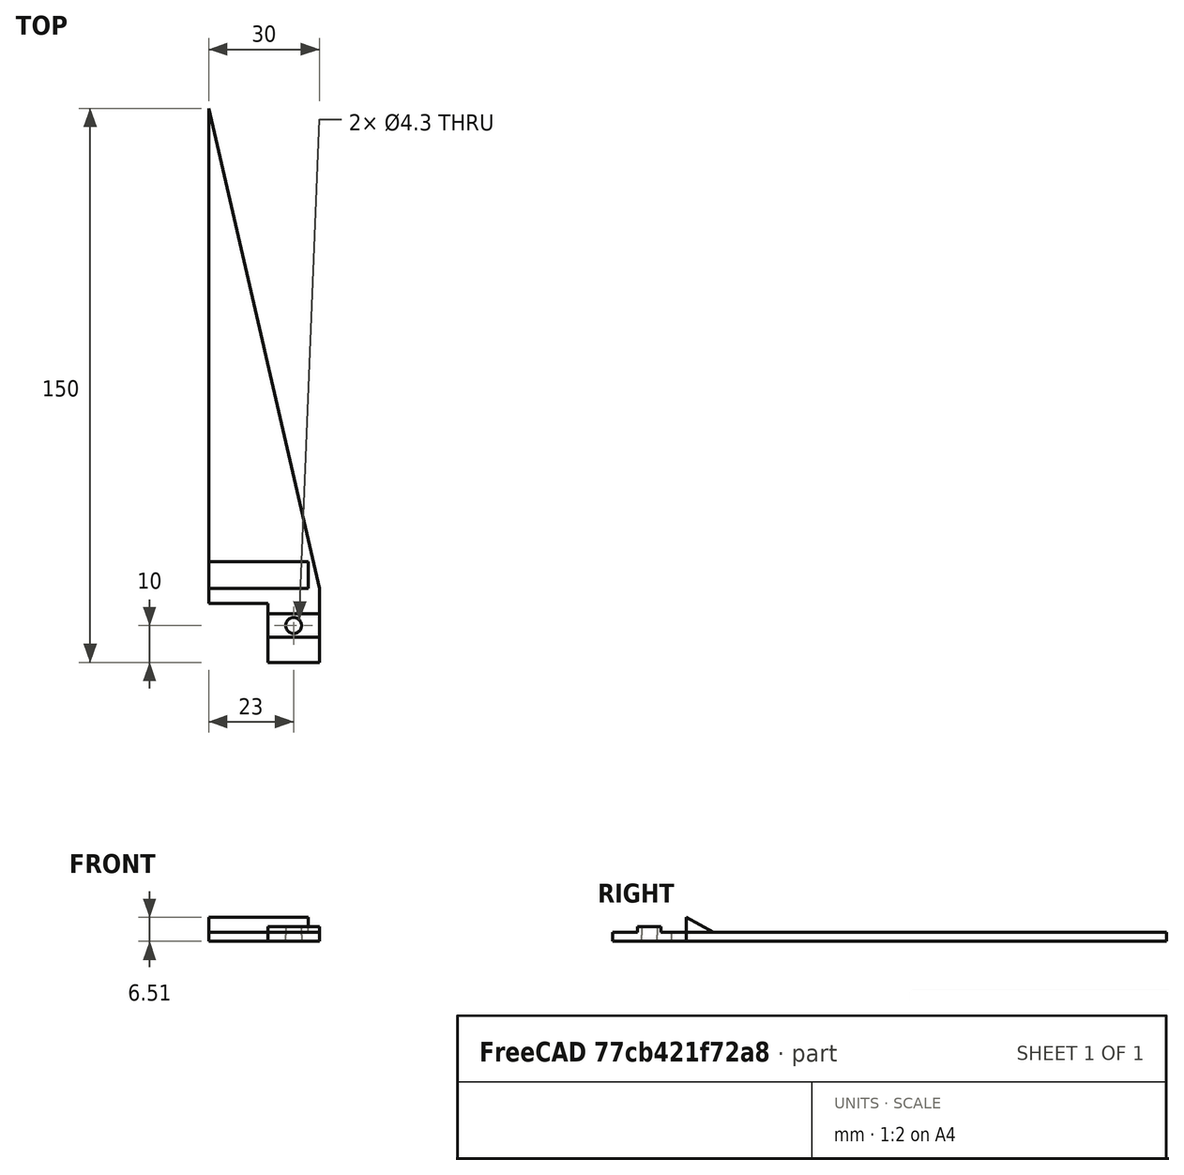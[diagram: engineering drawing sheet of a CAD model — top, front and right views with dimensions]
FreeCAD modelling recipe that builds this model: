
FCSTD DOCUMENT  (FreeCAD 0.19R)
Label: SimplePointe.r
License: All rights reserved
LicenseURL: http://en.wikipedia.org/wiki/All_rights_reserved
objects: Sketcher::SketchObject×6, PartDesign::Pad×3, PartDesign::Pocket×3, Mesh::Feature×2, PartDesign::Body×1
note: 19 computed .brp shape members not serialized (recipe doc carries the construction recipe); baked Part::Feature solids carry a one-line shape summary decoded from their .brp

FEATURE [Sketcher::SketchObject] Sketch
  FullyConstrained = true
  MapMode = 5
  Support = -> [XY_Plane]
  sketch-geometry (4):
    g0: LineSegment StartX=0 StartY=-20 StartZ=0 EndX=0 EndY=130 EndZ=0
    g1: LineSegment StartX=0 StartY=130 StartZ=0 EndX=30 EndY=0 EndZ=0
    g2: LineSegment StartX=30 StartY=0 StartZ=0 EndX=30 EndY=-20 EndZ=0
    g3: LineSegment StartX=30 StartY=-20 StartZ=0 EndX=0 EndY=-20 EndZ=0
  constraints (12):
    c: Vertical(g0)
    c: Coincident(g0,g1)
    c: PointOnObject(g1,g-1)
    c: Coincident(g1,g2)
    c: Coincident(g2,g3)
    c: Coincident(g3,g0)
    c: Horizontal(g3)
    c: Vertical(g2)
    c: Distance(g2) = 20
    c: PointOnObject(g0,g-2)
    c: Distance(g3) = 30
    c: Distance(g0) = 150
FEATURE [PartDesign::Pad] Pad
  Direction = (1,1,1)
  Length = 2.5
  Length2 = 100
  Profile = -> Sketch
  Type = 0
FEATURE [Sketcher::SketchObject] Sketch001
  FullyConstrained = false
  MapMode = 5
  Placement = pos=(0,0,2.5) rot=(0,0,1;0rad)
  Support = -> [Pad]
  sketch-geometry (4):
    g0: LineSegment StartX=-3.88556 StartY=-4 StartZ=0 EndX=16 EndY=-4 EndZ=0
    g1: LineSegment StartX=16 StartY=-4 StartZ=0 EndX=16 EndY=-24.7897 EndZ=0
    g2: LineSegment StartX=16 StartY=-24.7897 StartZ=0 EndX=-5.29231 EndY=-24.7897 EndZ=0
    g3: LineSegment StartX=-5.29231 StartY=-24.7897 StartZ=0 EndX=-3.88556 EndY=-4 EndZ=0
  constraints (9):
    c: Horizontal(g0)
    c: Coincident(g0,g1)
    c: Coincident(g1,g2)
    c: Horizontal(g2)
    c: Coincident(g2,g3)
    c: Coincident(g3,g0)
    c: DistanceX(g0) = 16
    c: DistanceY(g0) = -4
    c: Vertical(g1)
FEATURE [PartDesign::Pocket] Pocket
  BaseFeature = -> Pad
  Length = 5
  Length2 = 100
  Profile = -> Sketch001
  Type = 1
FEATURE [Sketcher::SketchObject] Sketch002
  FullyConstrained = true
  MapMode = 5
  Placement = pos=(0,0,2.5) rot=(0,0,1;0rad)
  Support = -> [Pocket]
  sketch-geometry (1):
    g0: Circle CenterX=23 CenterY=-10 CenterZ=0 NormalX=0 NormalY=0 NormalZ=1 AngleXU=0 Radius=2.15
  constraints (3):
    c: DistanceY(g0) = -10
    c: Diameter(g0) = 4.3
    c: DistanceX(g0) = 23
FEATURE [PartDesign::Pocket] Pocket001
  BaseFeature = -> Pocket
  Length = 5
  Length2 = 100
  Profile = -> Sketch002
  Type = 1
FEATURE [Sketcher::SketchObject] Sketch003
  FullyConstrained = false
  MapMode = 5
  Placement = pos=(0,0,0) rot=(0.57735,-0.57735,-0.57735;2.0944rad)
  Support = -> [Pocket001]
  sketch-geometry (3):
    g0: LineSegment StartX=0 StartY=6.51026 StartZ=0 EndX=-7.95 EndY=2.16643 EndZ=0
    g1: LineSegment StartX=-7.95 StartY=2.16643 StartZ=0 EndX=0 EndY=2.16643 EndZ=0
    g2: LineSegment StartX=0 StartY=2.16643 StartZ=0 EndX=0 EndY=6.51026 EndZ=0
  constraints (7):
    c: Coincident(g0,g1)
    c: Horizontal(g1)
    c: Coincident(g1,g2)
    c: Coincident(g2,g0)
    c: Vertical(g2)
    c: DistanceX(g1) = 0
    c: Distance(g1) = 7.95
FEATURE [PartDesign::Pad] Pad001
  BaseFeature = -> Pocket001
  Direction = (1,1,1)
  Length = 27
  Length2 = 100
  Profile = -> Sketch003
  Reversed = true
  Type = 0
FEATURE [Sketcher::SketchObject] Sketch004
  FullyConstrained = false
  MapMode = 5
  Placement = pos=(30,0,0) rot=(0.57735,0.57735,0.57735;2.0944rad)
  Support = -> [Pad001]
  sketch-geometry (5):
    g0: LineSegment StartX=-13.175 StartY=4 StartZ=0 EndX=-6.825 EndY=4 EndZ=0
    g1: LineSegment StartX=-6.825 StartY=4 StartZ=0 EndX=-6.825 EndY=1.71072 EndZ=0
    g2: LineSegment StartX=-6.825 StartY=1.71072 StartZ=0 EndX=-13.175 EndY=1.71072 EndZ=0
    g3: LineSegment StartX=-13.175 StartY=1.71072 StartZ=0 EndX=-13.175 EndY=4 EndZ=0
    g4: LineSegment StartX=-10 StartY=5.23731 StartZ=0 EndX=-10 EndY=2.74144 EndZ=0
  constraints (12):
    c: Coincident(g0,g1)
    c: Coincident(g1,g2)
    c: Coincident(g2,g3)
    c: Coincident(g3,g0)
    c: Horizontal(g0)
    c: Horizontal(g2)
    c: Vertical(g1)
    c: Vertical(g3)
    c: Distance(g0) = 6.35
    c: DistanceX(g4) = -10
    c: Symmetric(g0,g0,g4)
    c: DistanceY(g0) = 4
FEATURE [PartDesign::Pad] Pad002
  BaseFeature = -> Pad001
  Direction = (1,1,1)
  Length = 14
  Length2 = 100
  Profile = -> Sketch004
  Reversed = true
  Type = 0
FEATURE [Sketcher::SketchObject] Sketch005
  ExternalGeometry = -> [Pad002]
  FullyConstrained = true
  MapMode = 5
  Placement = pos=(0,0,1.71072) rot=(1,0,0;3.14159rad)
  Support = -> [Pad002]
  sketch-geometry (1):
    g0: Circle CenterX=23 CenterY=10 CenterZ=0 NormalX=0 NormalY=0 NormalZ=1 AngleXU=0 Radius=2.15
  constraints (2):
    c: Diameter(g0) = 4.3
    c: Coincident(g0,g-3)
FEATURE [PartDesign::Pocket] Pocket002
  BaseFeature = -> Pad002
  Length = 5
  Length2 = 100
  Profile = -> Sketch005
  Type = 0
FEATURE [PartDesign::Body] Body
  Group = -> [Sketch,Pad,Sketch001,Pocket,Sketch002,Pocket001,Sketch003,Pad001,Sketch004,Pad002,Sketch005,Pocket002]
  Origin = -> Origin
  Tip = -> Pocket002
FEATURE [Mesh::Feature] Mesh  label="Pocket002 (Meshed)"
FEATURE [Mesh::Feature] Mesh001  label="Pocket002 (Meshed)001"
